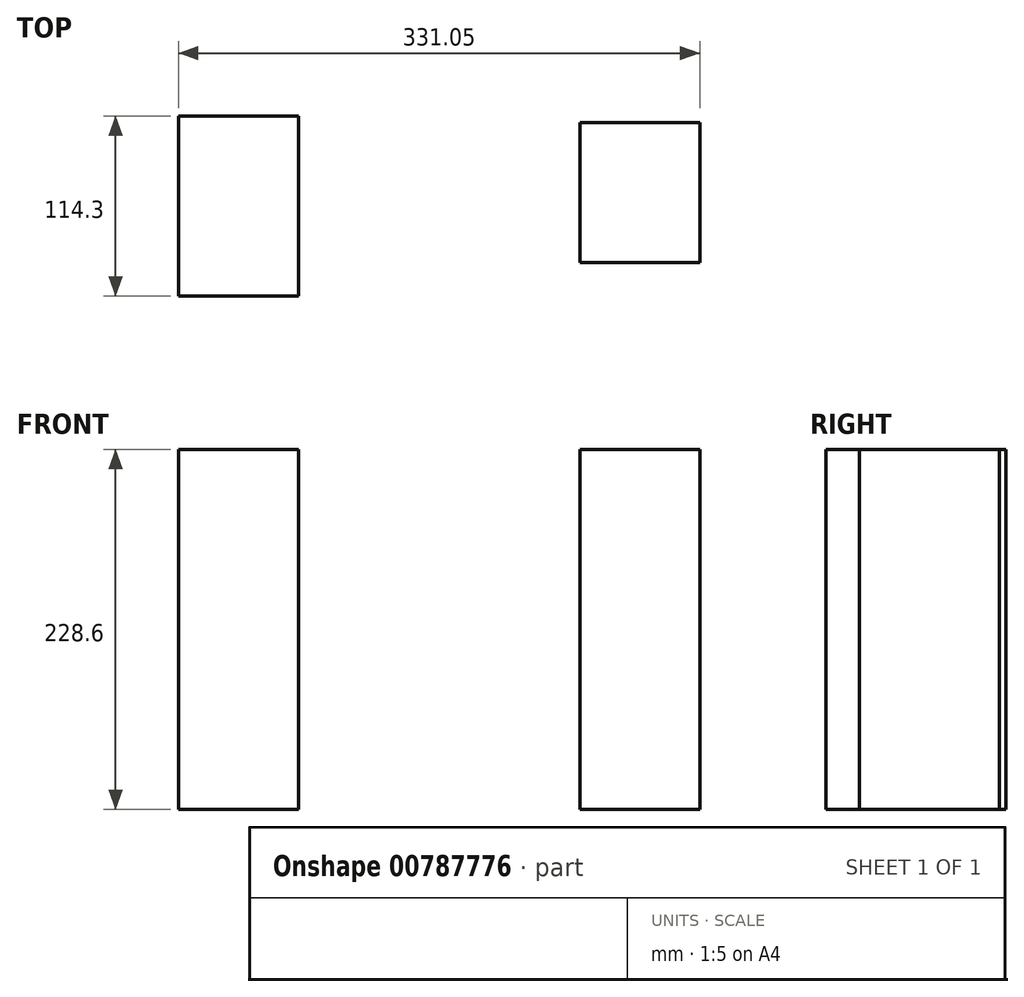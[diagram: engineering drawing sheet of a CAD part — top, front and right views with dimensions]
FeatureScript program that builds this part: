
annotation { "Feature Type Name" : "Feature", "Feature Type Description" : "" }
export const myFeature = defineFeature(function(context is Context, id is Id, definition is map)
    precondition{}
    {
        {
            var Q0;
            Q0=qCreatedBy(makeId("Top.planeOp"),FACE);
            var sketch = newSketch(context, id + "F0", { "sketchPlane" : qUnion([Q0])});
            skLineSegment(sketch, "E0.bottom", {"start": v(-38.1, 57.15) * mm, "end": v(38.1, 57.15) * mm});
            skLineSegment(sketch, "E0.top", {"start": v(-38.1, -57.15) * mm, "end": v(38.1, -57.15) * mm});
            skLineSegment(sketch, "E0.left", {"start": v(-38.1, 57.15) * mm, "end": v(-38.1, -57.15) * mm});
            skLineSegment(sketch, "E0.right", {"start": v(38.1, 57.15) * mm, "end": v(38.1, -57.15) * mm});
            skPoint(sketch, "E0.middle", {"position": v(0, 0) * mm});
            skSolve(sketch);
        }
        {
            var Q0;
            Q0 = qSketchRegion(id + "F0", true);
            extrude(context, id + "F1", {"entities" : qUnion([Q0]), "endBound" : BoundingType.SYMMETRIC, "depth" : 228.6 * mm, "offsetDistance" : 25.4 * mm});
        }
        {
            var Q0;
            Q0=qCreatedBy(makeId("Top.planeOp"),FACE);
            var sketch = newSketch(context, id + "F2", { "sketchPlane" : qUnion([Q0])});
            skLineSegment(sketch, "E1.bottom", {"start": v(292.95, -35.77) * mm, "end": v(216.75, -35.77) * mm});
            skLineSegment(sketch, "E1.top", {"start": v(292.95, 53.13) * mm, "end": v(216.75, 53.13) * mm});
            skLineSegment(sketch, "E1.left", {"start": v(292.95, -35.77) * mm, "end": v(292.95, 53.13) * mm});
            skLineSegment(sketch, "E1.right", {"start": v(216.75, -35.77) * mm, "end": v(216.75, 53.13) * mm});
            skPoint(sketch, "E1.middle", {"position": v(254.85, 8.68) * mm});
            skSolve(sketch);
        }
        {
            var Q0;
            Q0 = qSketchRegion(id + "F2", true);
            extrude(context, id + "F3", {"entities" : qUnion([Q0]), "endBound" : BoundingType.SYMMETRIC, "depth" : 228.6 * mm, "offsetDistance" : 25.4 * mm});
        }
    });
